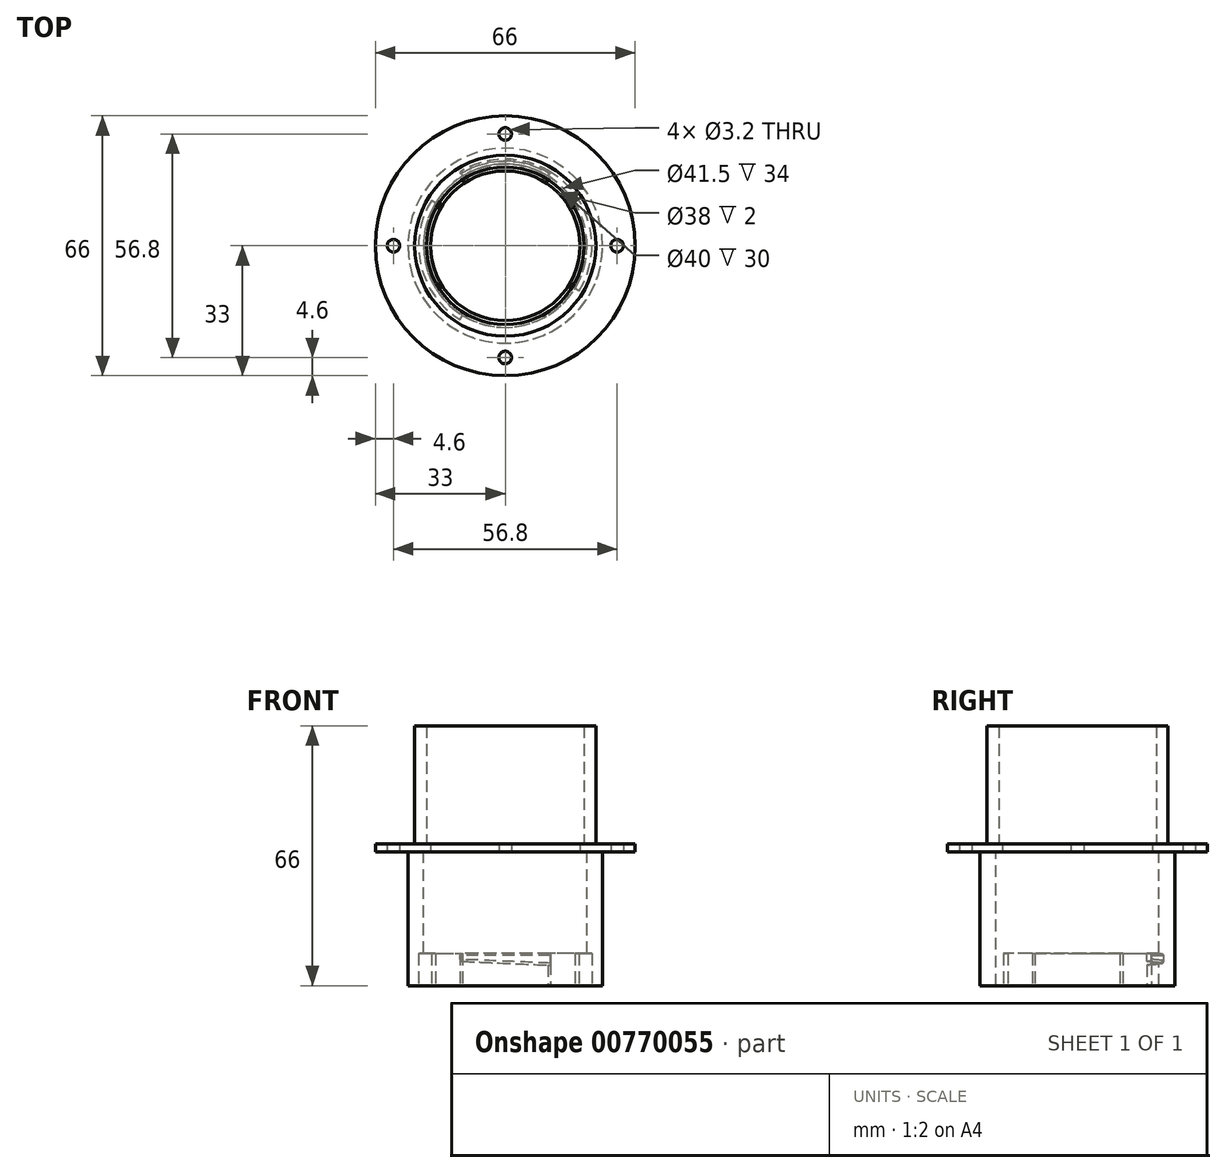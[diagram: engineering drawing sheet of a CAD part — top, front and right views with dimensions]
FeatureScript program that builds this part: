
annotation { "Feature Type Name" : "Feature", "Feature Type Description" : "" }
export const myFeature = defineFeature(function(context is Context, id is Id, definition is map)
    precondition{}
    {
        {
            var Q0;
            Q0=qCreatedBy(makeId("Top.planeOp"),FACE);
            var sketch = newSketch(context, id + "F0", { "sketchPlane" : qUnion([Q0])});
            skCircle(sketch, "E0", {"center": v(0, 0) * mm, "radius": 20.75 * mm});
            skCircle(sketch, "E1", {"center": v(0, 0) * mm, "radius": 18.75 * mm});
            skSolve(sketch);
        }
        {
            var Q0;
            Q0=makeQuery(id+"F0.imprint","IMPRINT",FACE,{"disambiguationData":[TD([[makeQuery(id+"F0.imprint","IMPRINT",EDGE,{"derivedFrom":sQuery(id+"F0.wireOp",EDGE,"E0")}),1.0]])]});
            extrude(context, id + "F1", {"entities" : qUnion([Q0]), "depth" : 34 * mm});
        }
        {
            var Q0;
            Q0=makeQuery(id+"F1.opExtrude","CAP_FACE",FACE,{"disambiguationData":[OSD([sQuery(id+"F0.wireOp",EDGE,"E0"),sQuery(id+"F0.wireOp",EDGE,"E1")])],"isStart":false});
            cPlane(context, id + "F2", {"entities" : qUnion([Q0]), "cplaneType" : CPlaneType.OFFSET, "offset" : 25.8 * mm, "oppositeDirection" : true, "width" : 150 * mm, "height" : 150 * mm});
        }
        {
            var Q0;
            Q0=qCreatedBy(id+"F2.planeOp",FACE);
            var sketch = newSketch(context, id + "F3", { "sketchPlane" : qUnion([Q0])});
            skCircle(sketch, "E2.0", {"center": v(0, 0) * mm, "radius": 20.75 * mm});
            skCircle(sketch, "E3", {"center": v(0, 0) * mm, "radius": 22 * mm});
            skLineSegment(sketch, "E4", {"start": v(-11.5, 18.75) * mm, "end": v(11.5, -18.75) * mm});
            skLineSegment(sketch, "E5", {"start": v(-11.5, -18.75) * mm, "end": v(11.5, 18.75) * mm});
            skLineSegment(sketch, "E6", {"start": v(-11.5, 18.75) * mm, "end": v(0, 21.22) * mm, "construction": true});
            skLineSegment(sketch, "E7", {"start": v(0, 21.22) * mm, "end": v(11.5, 18.75) * mm, "construction": true});
            skSolve(sketch);
        }
        {
            var Q0;
            {var subQ0=sQuery(id+"F3.wireOp",EDGE,"E4");var subQ1=sQuery(id+"F3.wireOp",EDGE,"E2.0");var subQ2=makeQuery(id+"F3.imprint","INTERSECT",VERTEX,{"disambiguationData":[OD(0.0)],"derivedFrom":[subQ1,subQ0]});Q0=makeQuery(id+"F3.imprint","IMPRINT",FACE,{"disambiguationData":[TD([[makeQuery(id+"F3.imprint","IMPRINT",EDGE,{"disambiguationData":[TD([[subQ2,1.0]])],"derivedFrom":subQ1}),-1.0]])]});}
            var Q1;
            {var subQ0=sQuery(id+"F3.wireOp",EDGE,"E5");var subQ1=sQuery(id+"F3.wireOp",EDGE,"E2.0");var subQ2=makeQuery(id+"F3.imprint","INTERSECT",VERTEX,{"disambiguationData":[OD(1.0)],"derivedFrom":[subQ1,subQ0]});Q1=makeQuery(id+"F3.imprint","IMPRINT",FACE,{"disambiguationData":[TD([[makeQuery(id+"F3.imprint","IMPRINT",EDGE,{"disambiguationData":[TD([[subQ2,-1.0]])],"derivedFrom":subQ1}),-1.0]])]});}
            extrude(context, id + "F4", {"entities" : qUnion([Q0, Q1]), "operationType" : NewBodyOperationType.ADD, "oppositeDirection" : true, "depth" : 3 * mm, "offsetDistance" : 25 * mm});
        }
        {
            var Q0;
            Q0=qCreatedBy(makeId("Front.planeOp"),FACE);
            cPlane(context, id + "F5", {"entities" : qUnion([Q0]), "cplaneType" : CPlaneType.OFFSET, "offset" : 25 * mm, "width" : 150 * mm, "height" : 150 * mm});
        }
        {
            var Q0;
            Q0=qCreatedBy(id+"F5.planeOp",FACE);
            var sketch = newSketch(context, id + "F6", { "sketchPlane" : qUnion([Q0])});
            skLineSegment(sketch, "E8.0.0", {"start": v(11.5, 8.2) * mm, "end": v(-11.5, 8.2) * mm});
            skLineSegment(sketch, "E8.0.1", {"start": v(-11.5, 8.2) * mm, "end": v(-11.5, 5.2) * mm});
            skLineSegment(sketch, "E8.0.2", {"start": v(-11.5, 5.2) * mm, "end": v(11.5, 5.2) * mm});
            skLineSegment(sketch, "E8.0.3", {"start": v(11.5, 5.2) * mm, "end": v(11.5, 8.2) * mm});
            skLineSegment(sketch, "E9", {"start": v(11.5, 6.2) * mm, "end": v(-11.5, 5.2) * mm});
            skSolve(sketch);
        }
        {
            var Q0;
            {var subQ0=sQuery(id+"F6.wireOp",EDGE,"E8.0.2");Q0=makeQuery(id+"F6.imprint","IMPRINT",FACE,{"disambiguationData":[TD([[makeQuery(id+"F6.imprint","IMPRINT",EDGE,{"derivedFrom":subQ0}),1.0]])]});}
            var Q1;
            Q1=makeQuery(id+"F1.opExtrude","SWEPT_FACE",FACE,{"disambiguationData":[OSD([sQuery(id+"F0.wireOp",EDGE,"E0")])]});
            extrude(context, id + "F7", {"entities" : qUnion([Q0]), "operationType" : NewBodyOperationType.REMOVE, "endBound" : BoundingType.UP_TO_SURFACE, "oppositeDirection" : true, "endBoundEntityFace" : qUnion([Q1]), "depth" : 25 * mm});
        }
        {
            var Q0;
            Q0=qCreatedBy(makeId("Front.planeOp"),FACE);
            cPlane(context, id + "F8", {"entities" : qUnion([Q0]), "cplaneType" : CPlaneType.OFFSET, "offset" : 25 * mm, "oppositeDirection" : true, "width" : 150 * mm, "height" : 150 * mm});
        }
        {
            var Q0;
            Q0=qCreatedBy(id+"F8.planeOp",FACE);
            var sketch = newSketch(context, id + "F9", { "sketchPlane" : qUnion([Q0])});
            skLineSegment(sketch, "E10.0.0", {"start": v(-11.5, 8.2) * mm, "end": v(11.5, 8.2) * mm});
            skLineSegment(sketch, "E10.0.1", {"start": v(11.5, 8.2) * mm, "end": v(11.5, 5.2) * mm});
            skLineSegment(sketch, "E10.0.2", {"start": v(11.5, 5.2) * mm, "end": v(-11.5, 5.2) * mm});
            skLineSegment(sketch, "E10.0.3", {"start": v(-11.5, 5.2) * mm, "end": v(-11.5, 8.2) * mm});
            skLineSegment(sketch, "E11", {"start": v(11.5, 5.2) * mm, "end": v(-11.5, 6.2) * mm});
            skSolve(sketch);
        }
        {
            var Q0;
            {var subQ0=sQuery(id+"F9.wireOp",EDGE,"E10.0.2");Q0=makeQuery(id+"F9.imprint","IMPRINT",FACE,{"disambiguationData":[TD([[makeQuery(id+"F9.imprint","IMPRINT",EDGE,{"derivedFrom":subQ0}),-1.0]])]});}
            var Q1;
            Q1=makeQuery(id+"F7.boolean.opBoolean","MERGE",FACE,{"derivedFrom":[makeQuery(id+"F1.opExtrude","SWEPT_FACE",FACE,{"disambiguationData":[OSD([sQuery(id+"F0.wireOp",EDGE,"E0")])]})],"fromTools":[makeQuery(id+"F7.opExtrude","CAP_FACE",FACE,{"disambiguationData":[OSD([sQuery(id+"F6.wireOp",EDGE,"E8.0.2"),sQuery(id+"F6.wireOp",EDGE,"E8.0.3"),sQuery(id+"F6.wireOp",EDGE,"E9")])],"isStart":false})]});
            extrude(context, id + "F10", {"entities" : qUnion([Q0]), "operationType" : NewBodyOperationType.REMOVE, "endBound" : BoundingType.UP_TO_SURFACE, "endBoundEntityFace" : qUnion([Q1]), "depth" : 25 * mm});
        }
        {
            var Q0;
            Q0=makeQuery(id+"F1.opExtrude","CAP_FACE",FACE,{"disambiguationData":[OSD([sQuery(id+"F0.wireOp",EDGE,"E0"),sQuery(id+"F0.wireOp",EDGE,"E1")])],"isStart":true});
            var sketch = newSketch(context, id + "F11", { "sketchPlane" : qUnion([Q0])});
            skCircle(sketch, "E12", {"center": v(0, 0) * mm, "radius": 24.25 * mm});
            skSolve(sketch);
        }
        {
            var Q0;
            Q0=makeQuery(id+"F11.imprint","IMPRINT",FACE,{"disambiguationData":[TD([[makeQuery(id+"F11.imprint","IMPRINT",EDGE,{"derivedFrom":sQuery(id+"F11.wireOp",EDGE,"E12")}),1.0]])]});
            var Q1;
            Q1=makeQuery(id+"F11.imprint","IMPRINT",FACE,{"disambiguationData":[TD([[makeQuery(id+"F11.imprint","IMPRINT",EDGE,{"derivedFrom":makeQuery(id+"F1.opExtrude","CAP_EDGE",EDGE,{"disambiguationData":[OSD([sQuery(id+"F0.wireOp",EDGE,"E0")])],"isStart":true})}),-1.0]])]});
            extrude(context, id + "F12", {"entities" : qUnion([Q0, Q1]), "operationType" : NewBodyOperationType.ADD, "depth" : 3 * mm});
        }
        {
            var Q0;
            Q0=makeQuery(id+"F12.opExtrude","CAP_FACE",FACE,{"disambiguationData":[OSD([sQuery(id+"F0.wireOp",EDGE,"E1"),sQuery(id+"F11.wireOp",EDGE,"E12")])],"isStart":false});
            var sketch = newSketch(context, id + "F13", { "sketchPlane" : qUnion([Q0])});
            skCircle(sketch, "E13.0", {"center": v(0, 0) * mm, "radius": 20.75 * mm});
            skCircle(sketch, "E14", {"center": v(0, 0) * mm, "radius": 16.75 * mm});
            skCircle(sketch, "E15.0", {"center": v(0, 0) * mm, "radius": 18.75 * mm});
            skSolve(sketch);
        }
        {
            var Q0;
            Q0=makeQuery(id+"F13.imprint","IMPRINT",FACE,{"disambiguationData":[TD([[makeQuery(id+"F13.imprint","IMPRINT",EDGE,{"derivedFrom":sQuery(id+"F13.wireOp",EDGE,"E14")}),-1.0]])]});
            extrude(context, id + "F14", {"entities" : qUnion([Q0]), "operationType" : NewBodyOperationType.ADD, "oppositeDirection" : true, "depth" : 3 * mm});
        }
        {
            var Q0;
            Q0=makeQuery(id+"F13.imprint","IMPRINT",FACE,{"disambiguationData":[TD([[makeQuery(id+"F13.imprint","IMPRINT",EDGE,{"derivedFrom":sQuery(id+"F13.wireOp",EDGE,"E13.0")}),1.0]])]});
            extrude(context, id + "F15", {"entities" : qUnion([Q0]), "operationType" : NewBodyOperationType.ADD, "depth" : 35 * mm});
        }
        {
            var Q0;
            Q0=makeQuery(id+"F1.opExtrude","CAP_EDGE",EDGE,{"disambiguationData":[OSD([sQuery(id+"F0.wireOp",EDGE,"E0")])],"isStart":false});
            var Q1;
            Q1=makeQuery(id+"F1.opExtrude","CAP_EDGE",EDGE,{"disambiguationData":[OSD([sQuery(id+"F0.wireOp",EDGE,"E1")])],"isStart":false});
            var Q2;
            {var subQ0=sQuery(id+"F3.wireOp",EDGE,"E3");Q2=makeQuery(id+"F4.opExtrude","CAP_EDGE",EDGE,{"disambiguationData":[OSD([subQ0]),TDD([makeQuery(id+"F3.imprint","IMPRINT",EDGE,{"disambiguationData":[TD([[makeQuery(id+"F3.imprint","INTERSECT",VERTEX,{"disambiguationData":[OD(1.0)],"derivedFrom":[subQ0,sQuery(id+"F3.wireOp",EDGE,"E4")]}),1.0]])],"derivedFrom":subQ0})])],"isStart":true});}
            var Q3;
            {var subQ0=sQuery(id+"F3.wireOp",EDGE,"E3");Q3=makeQuery(id+"F7.boolean.opBoolean","INTERSECT",EDGE,{"derivedFrom":[makeQuery(id+"F4.opExtrude","SWEPT_FACE",FACE,{"disambiguationData":[OSD([subQ0]),TDD([makeQuery(id+"F3.imprint","IMPRINT",EDGE,{"disambiguationData":[TD([[makeQuery(id+"F3.imprint","INTERSECT",VERTEX,{"disambiguationData":[OD(1.0)],"derivedFrom":[subQ0,sQuery(id+"F3.wireOp",EDGE,"E4")]}),1.0]])],"derivedFrom":subQ0})])]}),makeQuery(id+"F7.opExtrude","SWEPT_FACE",FACE,{"disambiguationData":[OSD([sQuery(id+"F6.wireOp",EDGE,"E9")])]})]});}
            var Q4;
            {var subQ0=sQuery(id+"F3.wireOp",EDGE,"E3");Q4=makeQuery(id+"F4.opExtrude","CAP_EDGE",EDGE,{"disambiguationData":[OSD([subQ0]),TDD([makeQuery(id+"F3.imprint","IMPRINT",EDGE,{"disambiguationData":[TD([[makeQuery(id+"F3.imprint","INTERSECT",VERTEX,{"disambiguationData":[OD(0.0)],"derivedFrom":[subQ0,sQuery(id+"F3.wireOp",EDGE,"E4")]}),1.0]])],"derivedFrom":subQ0})])],"isStart":true});}
            var Q5;
            {var subQ0=sQuery(id+"F3.wireOp",EDGE,"E3");Q5=makeQuery(id+"F10.boolean.opBoolean","INTERSECT",EDGE,{"derivedFrom":[makeQuery(id+"F4.opExtrude","SWEPT_FACE",FACE,{"disambiguationData":[OSD([subQ0]),TDD([makeQuery(id+"F3.imprint","IMPRINT",EDGE,{"disambiguationData":[TD([[makeQuery(id+"F3.imprint","INTERSECT",VERTEX,{"disambiguationData":[OD(0.0)],"derivedFrom":[subQ0,sQuery(id+"F3.wireOp",EDGE,"E4")]}),1.0]])],"derivedFrom":subQ0})])]}),makeQuery(id+"F10.opExtrude","SWEPT_FACE",FACE,{"disambiguationData":[OSD([sQuery(id+"F9.wireOp",EDGE,"E11")])]})]});}
            var Q6;
            Q6=makeQuery(id+"F1.opExtrude","CAP_EDGE",EDGE,{"disambiguationData":[OSD([sQuery(id+"F0.wireOp",EDGE,"E0")])],"isStart":true});
            chamfer(context, id + "F16", {"entities" : qUnion([Q0, Q1, Q2, Q3, Q4, Q5, Q6]), "width" : 0.5 * mm, "tangentPropagation" : true});
        }
        {
            var Q0;
            Q0=makeQuery(id+"F14.opExtrude","CAP_EDGE",EDGE,{"disambiguationData":[OSD([sQuery(id+"F13.wireOp",EDGE,"E14")])],"isStart":true});
            var Q1;
            Q1=makeQuery(id+"F14.opExtrude","CAP_EDGE",EDGE,{"disambiguationData":[OSD([sQuery(id+"F13.wireOp",EDGE,"E14")])],"isStart":false});
            var Q2;
            Q2=makeQuery(id+"F15.opExtrude","CAP_EDGE",EDGE,{"disambiguationData":[OSD([sQuery(id+"F13.wireOp",EDGE,"E13.0")])],"isStart":true});
            var Q3;
            Q3=makeQuery(id+"F12.opExtrude","CAP_EDGE",EDGE,{"disambiguationData":[OSD([sQuery(id+"F11.wireOp",EDGE,"E12")])],"isStart":false});
            var Q4;
            Q4=makeQuery(id+"F12.opExtrude","CAP_EDGE",EDGE,{"disambiguationData":[OSD([sQuery(id+"F11.wireOp",EDGE,"E12")])],"isStart":true});
            fillet(context, id + "F17", {"entities" : qUnion([Q0, Q1, Q2, Q3, Q4]), "radius" : 1.5 * mm, "tangentPropagation" : true, "allowEdgeOverflow" : false});
        }
        {
            var Q0;
            Q0=makeQuery(id+"F1.opExtrude","CAP_FACE",FACE,{"disambiguationData":[OSD([sQuery(id+"F0.wireOp",EDGE,"E0"),sQuery(id+"F0.wireOp",EDGE,"E1")])],"isStart":false});
            var sketch = newSketch(context, id + "F18", { "sketchPlane" : qUnion([Q0])});
            skCircle(sketch, "E16", {"center": v(0, 0) * mm, "radius": 24.75 * mm});
            skCircle(sketch, "E17.0", {"center": v(0, 0) * mm, "radius": 20.75 * mm});
            skSolve(sketch);
        }
        {
            var Q0;
            Q0=makeQuery(id+"F18.imprint","IMPRINT",FACE,{"disambiguationData":[TD([[makeQuery(id+"F18.imprint","IMPRINT",EDGE,{"derivedFrom":sQuery(id+"F18.wireOp",EDGE,"E16")}),1.0]])]});
            var Q1;
            Q1=makeQuery(id+"F12.opExtrude","CAP_FACE",FACE,{"disambiguationData":[OSD([sQuery(id+"F0.wireOp",EDGE,"E1"),sQuery(id+"F11.wireOp",EDGE,"E12")])],"isStart":true});
            extrude(context, id + "F19", {"entities" : qUnion([Q0]), "endBound" : BoundingType.UP_TO_SURFACE, "oppositeDirection" : true, "endBoundEntityFace" : qUnion([Q1]), "depth" : 35 * mm});
        }
        {
            var Q0;
            Q0=makeQuery(id+"F1.opExtrude","SWEPT_BODY",BODY,{"disambiguationData":[OSD([sQuery(id+"F0.wireOp",EDGE,"E0"),sQuery(id+"F0.wireOp",EDGE,"E1")])]});
            var Q1;
            Q1=makeQuery(id+"F19.opExtrude","SWEPT_BODY",BODY,{"disambiguationData":[OSD([sQuery(id+"F18.wireOp",EDGE,"E16"),sQuery(id+"F18.wireOp",EDGE,"E17.0")])]});
            booleanBodies(context, id + "F20", {"operationType" : BooleanOperationType.SUBTRACTION, "tools" : qUnion([Q0]), "targets" : qUnion([Q1])});
        }
        {
            var Q0;
            Q0=makeQuery(id+"F19.opExtrude","CAP_FACE",FACE,{"disambiguationData":[OSD([sQuery(id+"F18.wireOp",EDGE,"E16"),sQuery(id+"F18.wireOp",EDGE,"E17.0")])],"isStart":false});
            var sketch = newSketch(context, id + "F21", { "sketchPlane" : qUnion([Q0])});
            skLineSegment(sketch, "E18.0.0", {"start": v(-11.23, 18.32) * mm, "end": v(-10.85, 17.69) * mm});
            skLineSegment(sketch, "E18.0.2", {"start": v(-10.85, 17.69) * mm, "end": v(-11.24, 18.33) * mm});
            skLineSegment(sketch, "E18.0.3", {"start": v(-11.5, 18.75) * mm, "end": v(-11.24, 18.33) * mm});
            skFitSpline(sketch, "E18.0.5", {"points": [v(-11.5, 18.76) * mm, v(-11.41, 18.61) * mm, v(-11.32, 18.47) * mm, v(-11.23, 18.32) * mm]});
            skLineSegment(sketch, "E19.0.0", {"start": v(11.23, -18.32) * mm, "end": v(10.85, -17.69) * mm});
            skLineSegment(sketch, "E19.0.2", {"start": v(10.85, -17.69) * mm, "end": v(11.24, -18.33) * mm});
            skLineSegment(sketch, "E19.0.3", {"start": v(11.24, -18.33) * mm, "end": v(11.5, -18.75) * mm});
            skFitSpline(sketch, "E19.0.5", {"points": [v(11.5, -18.76) * mm, v(11.41, -18.61) * mm, v(11.32, -18.47) * mm, v(11.23, -18.32) * mm]});
            skCircle(sketch, "E20", {"center": v(0, 0) * mm, "radius": 20.75 * mm});
            skCircle(sketch, "E21", {"center": v(0, 0) * mm, "radius": 22 * mm});
            skLineSegment(sketch, "E22", {"start": v(18.76, 11.5) * mm, "end": v(0, 0) * mm});
            skLineSegment(sketch, "E23", {"start": v(0, 0) * mm, "end": v(-18.76, -11.5) * mm});
            skSolve(sketch);
        }
        {
            var Q0;
            {var subQ0=sQuery(id+"F21.wireOp",EDGE,"E19.0.5");var subQ3=makeQuery(id+"F21.imprint","IMPRINT",VERTEX,{"derivedFrom":subQ0});Q0=makeQuery(id+"F21.imprint","IMPRINT",FACE,{"disambiguationData":[TD([[makeQuery(id+"F21.imprint","IMPRINT",EDGE,{"disambiguationData":[TD([[subQ3,1.0]])],"derivedFrom":subQ0}),-1.0]])]});}
            var Q1;
            {var subQ0=sQuery(id+"F21.wireOp",EDGE,"E20");var subQ1=sQuery(id+"F21.wireOp",EDGE,"E19.0.2");var subQ2=makeQuery(id+"F21.imprint","INTERSECT",VERTEX,{"derivedFrom":[subQ1,subQ0]});Q1=makeQuery(id+"F21.imprint","IMPRINT",FACE,{"disambiguationData":[TD([[makeQuery(id+"F21.imprint","IMPRINT",EDGE,{"disambiguationData":[TD([[subQ2,-1.0]])],"derivedFrom":subQ0}),-1.0]])]});}
            var Q2;
            {var subQ1=sQuery(id+"F21.wireOp",EDGE,"E18.0.5");var subQ5=makeQuery(id+"F21.imprint","IMPRINT",VERTEX,{"derivedFrom":subQ1});Q2=makeQuery(id+"F21.imprint","IMPRINT",FACE,{"disambiguationData":[TD([[makeQuery(id+"F21.imprint","IMPRINT",EDGE,{"disambiguationData":[TD([[subQ5,1.0]])],"derivedFrom":subQ1}),-1.0]])]});}
            var Q3;
            {var subQ0=sQuery(id+"F21.wireOp",EDGE,"E20");var subQ1=sQuery(id+"F21.wireOp",EDGE,"E18.0.2");var subQ2=makeQuery(id+"F21.imprint","INTERSECT",VERTEX,{"derivedFrom":[subQ1,subQ0]});Q3=makeQuery(id+"F21.imprint","IMPRINT",FACE,{"disambiguationData":[TD([[makeQuery(id+"F21.imprint","IMPRINT",EDGE,{"disambiguationData":[TD([[subQ2,-1.0]])],"derivedFrom":subQ0}),-1.0]])]});}
            var Q4;
            {var subQ0=sQuery(id+"F3.wireOp",EDGE,"E5");var subQ1=sQuery(id+"F3.wireOp",EDGE,"E3");var subQ2=makeQuery(id+"F3.imprint","INTERSECT",VERTEX,{"disambiguationData":[OD(1.0)],"derivedFrom":[subQ1,subQ0]});var subQ3=sQuery(id+"F3.wireOp",EDGE,"E2.0");var subQ5=sQuery(id+"F3.wireOp",EDGE,"E4");var subQ6=makeQuery(id+"F3.imprint","INTERSECT",VERTEX,{"disambiguationData":[OD(0.0)],"derivedFrom":[subQ1,subQ5]});var subQ7=makeQuery(id+"F3.imprint","INTERSECT",VERTEX,{"disambiguationData":[OD(0.0)],"derivedFrom":[subQ3,subQ5]});Q4=makeQuery(id+"F20.opBoolean","COPY",FACE,{"derivedFrom":makeQuery(id+"F4.opExtrude","CAP_FACE",FACE,{"disambiguationData":[OSD([subQ3,subQ1,subQ5,subQ0]),TDD([makeQuery(id+"F3.imprint","IMPRINT",EDGE,{"disambiguationData":[TD([[subQ7,1.0]])],"derivedFrom":subQ3}),makeQuery(id+"F3.imprint","IMPRINT",EDGE,{"disambiguationData":[TD([[subQ6,1.0]])],"derivedFrom":subQ1}),makeQuery(id+"F3.imprint","IMPRINT",EDGE,{"disambiguationData":[TD([[subQ6,-1.0]])],"derivedFrom":subQ5}),makeQuery(id+"F3.imprint","IMPRINT",EDGE,{"disambiguationData":[TD([[subQ2,1.0]])],"derivedFrom":subQ0})])],"isStart":true})});}
            extrude(context, id + "F22", {"entities" : qUnion([Q0, Q1, Q2, Q3]), "operationType" : NewBodyOperationType.REMOVE, "endBound" : BoundingType.UP_TO_SURFACE, "oppositeDirection" : true, "endBoundEntityFace" : qUnion([Q4]), "depth" : 25 * mm, "offsetDistance" : 25 * mm});
        }
        {
            var Q0;
            Q0=makeQuery(id+"F19.opExtrude","CAP_FACE",FACE,{"disambiguationData":[OSD([sQuery(id+"F18.wireOp",EDGE,"E16"),sQuery(id+"F18.wireOp",EDGE,"E17.0")])],"isStart":true});
            var sketch = newSketch(context, id + "F23", { "sketchPlane" : qUnion([Q0])});
            skCircle(sketch, "E24.0", {"center": v(0, 0) * mm, "radius": 19 * mm});
            skCircle(sketch, "E25", {"center": v(0, 0) * mm, "radius": 33 * mm});
            skCircle(sketch, "E26", {"center": v(0, 0) * mm, "radius": 23 * mm});
            skCircle(sketch, "E27", {"center": v(0, 28.4) * mm, "radius": 1.6 * mm});
            skCircle(sketch, "E28", {"center": v(28.4, 0) * mm, "radius": 1.6 * mm});
            skCircle(sketch, "E29", {"center": v(0, -28.4) * mm, "radius": 1.6 * mm});
            skCircle(sketch, "E30", {"center": v(-28.4, 0) * mm, "radius": 1.6 * mm});
            skLineSegment(sketch, "E31", {"start": v(0, 28.4) * mm, "end": v(0, -28.4) * mm, "construction": true});
            skLineSegment(sketch, "E32", {"start": v(-28.4, 0) * mm, "end": v(28.4, 0) * mm, "construction": true});
            skCircle(sketch, "E33.0", {"center": v(0, 0) * mm, "radius": 20.75 * mm});
            skSolve(sketch);
        }
        {
            var Q0;
            Q0=makeQuery(id+"F23.imprint","IMPRINT",FACE,{"disambiguationData":[TD([[makeQuery(id+"F23.imprint","IMPRINT",EDGE,{"derivedFrom":sQuery(id+"F23.wireOp",EDGE,"E25")}),1.0]])]});
            var Q1;
            Q1=makeQuery(id+"F23.imprint","IMPRINT",FACE,{"disambiguationData":[TD([[makeQuery(id+"F23.imprint","IMPRINT",EDGE,{"derivedFrom":sQuery(id+"F23.wireOp",EDGE,"E26")}),-1.0]])]});
            var Q2;
            Q2=makeQuery(id+"F23.imprint","IMPRINT",FACE,{"disambiguationData":[TD([[makeQuery(id+"F23.imprint","IMPRINT",EDGE,{"derivedFrom":sQuery(id+"F23.wireOp",EDGE,"E26")}),1.0]])]});
            var Q3;
            Q3=makeQuery(id+"F23.imprint","IMPRINT",FACE,{"disambiguationData":[TD([[makeQuery(id+"F23.imprint","IMPRINT",EDGE,{"derivedFrom":sQuery(id+"F23.wireOp",EDGE,"E24.0")}),-1.0]])]});
            extrude(context, id + "F24", {"entities" : qUnion([Q0, Q1, Q2, Q3]), "operationType" : NewBodyOperationType.ADD, "depth" : 2 * mm, "offsetDistance" : 25 * mm});
        }
        {
            var Q0;
            Q0=makeQuery(id+"F24.opExtrude","CAP_FACE",FACE,{"disambiguationData":[OSD([sQuery(id+"F23.wireOp",EDGE,"E24.0"),sQuery(id+"F23.wireOp",EDGE,"E25"),sQuery(id+"F23.wireOp",EDGE,"E27"),sQuery(id+"F23.wireOp",EDGE,"E28"),sQuery(id+"F23.wireOp",EDGE,"E29"),sQuery(id+"F23.wireOp",EDGE,"E30")])],"isStart":false});
            var sketch = newSketch(context, id + "F25", { "sketchPlane" : qUnion([Q0])});
            skCircle(sketch, "E34.0", {"center": v(0, 0) * mm, "radius": 19 * mm});
            skCircle(sketch, "E35", {"center": v(0, 0) * mm, "radius": 20 * mm});
            skCircle(sketch, "E36", {"center": v(0, 0) * mm, "radius": 23 * mm});
            skSolve(sketch);
        }
        {
            var Q0;
            Q0=makeQuery(id+"F25.imprint","IMPRINT",FACE,{"disambiguationData":[TD([[makeQuery(id+"F25.imprint","IMPRINT",EDGE,{"derivedFrom":sQuery(id+"F25.wireOp",EDGE,"E35")}),-1.0]])]});
            extrude(context, id + "F26", {"entities" : qUnion([Q0]), "operationType" : NewBodyOperationType.ADD, "depth" : 30 * mm, "offsetDistance" : 25 * mm});
        }
    });
